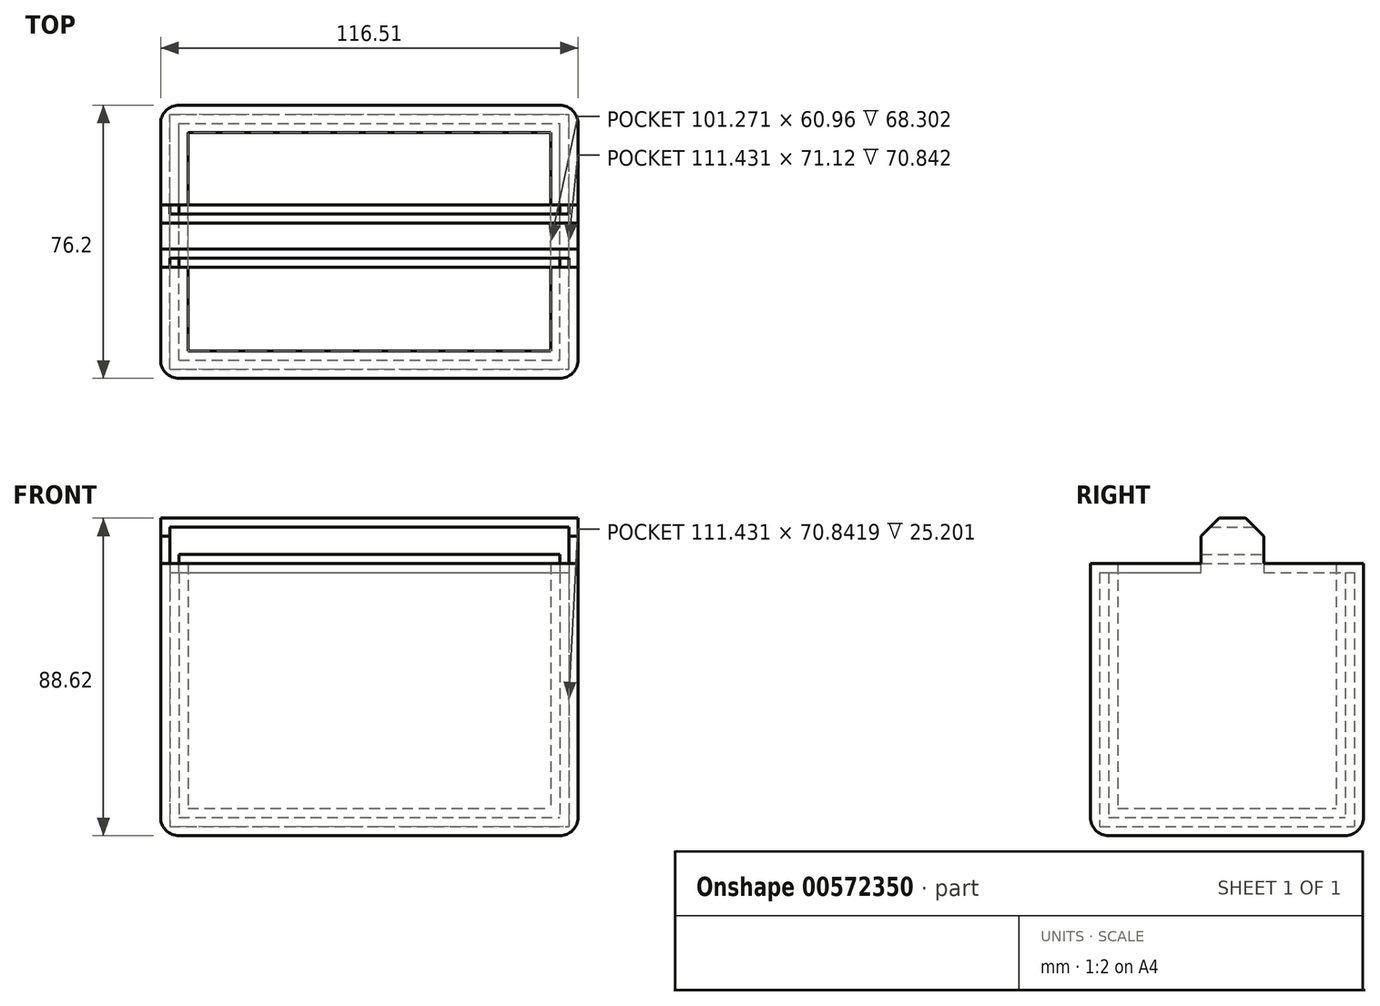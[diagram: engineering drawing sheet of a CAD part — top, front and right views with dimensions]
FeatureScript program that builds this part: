
annotation { "Feature Type Name" : "Feature", "Feature Type Description" : "" }
export const myFeature = defineFeature(function(context is Context, id is Id, definition is map)
    precondition{}
    {
        {
            var Q0;
            Q0=qCreatedBy(makeId("Front.planeOp"),FACE);
            var sketch = newSketch(context, id + "F0", { "sketchPlane" : qUnion([Q0])});
            skLineSegment(sketch, "E0.bottom", {"start": v(-51.4, 55.19) * mm, "end": v(65.12, 55.19) * mm});
            skLineSegment(sketch, "E0.top", {"start": v(-51.4, -20.73) * mm, "end": v(65.12, -20.73) * mm});
            skLineSegment(sketch, "E0.left", {"start": v(-51.4, 55.19) * mm, "end": v(-51.4, -20.73) * mm});
            skLineSegment(sketch, "E0.right", {"start": v(65.12, 55.19) * mm, "end": v(65.12, -20.73) * mm});
            skSolve(sketch);
        }
        {
            var Q0;
            Q0=makeQuery(id+"F0.imprint","IMPRINT",FACE,{"disambiguationData":[TD([[makeQuery(id+"F0.imprint","IMPRINT",EDGE,{"derivedFrom":sQuery(id+"F0.wireOp",EDGE,"E0.bottom")}),-1.0]])]});
            extrude(context, id + "F1", {"entities" : qUnion([Q0]), "depth" : 76.2 * mm, "offsetDistance" : 25.4 * mm});
        }
        {
            var Q0;
            Q0=makeQuery(id+"F1.opExtrude","SWEPT_FACE",FACE,{"disambiguationData":[OSD([sQuery(id+"F0.wireOp",EDGE,"E0.bottom")])]});
            shell(context, id + "F2", {"entities" : qUnion([Q0]), "thickness" : 7.62 * mm});
        }
        {
            var Q0;
            Q0=makeQuery(id+"F1.opExtrude","SWEPT_FACE",FACE,{"disambiguationData":[OSD([sQuery(id+"F0.wireOp",EDGE,"E0.bottom")])]});
            var sketch = newSketch(context, id + "F3", { "sketchPlane" : qUnion([Q0])});
            skLineSegment(sketch, "E1.bottom", {"start": v(-51.4, -27.74) * mm, "end": v(65.12, -27.74) * mm});
            skLineSegment(sketch, "E1.top", {"start": v(-51.4, -45.26) * mm, "end": v(65.12, -45.26) * mm});
            skLineSegment(sketch, "E1.left", {"start": v(-51.4, -27.74) * mm, "end": v(-51.4, -45.26) * mm});
            skLineSegment(sketch, "E1.right", {"start": v(65.12, -27.74) * mm, "end": v(65.12, -45.26) * mm});
            skSolve(sketch);
        }
        {
            var Q0;
            Q0 = qSketchRegion(id + "F3", true);
            extrude(context, id + "F4", {"entities" : qUnion([Q0]), "operationType" : NewBodyOperationType.ADD, "depth" : 12.7 * mm, "offsetDistance" : 25.4 * mm});
        }
        {
            var Q0;
            Q0=makeQuery(id+"F4.opExtrude","SWEPT_FACE",FACE,{"disambiguationData":[OSD([sQuery(id+"F3.wireOp",EDGE,"E1.top")])]});
            var Q1;
            Q1=makeQuery(id+"F4.opExtrude","SWEPT_FACE",FACE,{"disambiguationData":[OSD([sQuery(id+"F3.wireOp",EDGE,"E1.bottom")])]});
            shell(context, id + "F5", {"entities" : qUnion([Q0, Q1]), "thickness" : 2.54 * mm});
        }
        {
            var Q0;
            Q0=makeQuery(id+"F1.opExtrude","CAP_EDGE",EDGE,{"disambiguationData":[OSD([sQuery(id+"F0.wireOp",EDGE,"E0.right")])],"isStart":true});
            fillet(context, id + "F6", {"entities" : qUnion([Q0]), "radius" : 5.08 * mm, "tangentPropagation" : true, "allowEdgeOverflow" : false});
        }
        {
            var Q0;
            Q0=makeQuery(id+"F1.opExtrude","CAP_EDGE",EDGE,{"disambiguationData":[OSD([sQuery(id+"F0.wireOp",EDGE,"E0.top")])],"isStart":true});
            var Q1;
            Q1=makeQuery(id+"F1.opExtrude","CAP_EDGE",EDGE,{"disambiguationData":[OSD([sQuery(id+"F0.wireOp",EDGE,"E0.left")])],"isStart":true});
            fillet(context, id + "F7", {"entities" : qUnion([Q0, Q1]), "radius" : 5.08 * mm, "tangentPropagation" : true, "allowEdgeOverflow" : false});
        }
        {
            var Q0;
            Q0=makeQuery(id+"F1.opExtrude","CAP_EDGE",EDGE,{"disambiguationData":[OSD([sQuery(id+"F0.wireOp",EDGE,"E0.left")])],"isStart":false});
            fillet(context, id + "F8", {"entities" : qUnion([Q0]), "radius" : 5.08 * mm, "tangentPropagation" : true, "allowEdgeOverflow" : false});
        }
        {
            var Q0;
            Q0=makeQuery(id+"F1.opExtrude","SWEPT_EDGE",EDGE,{"disambiguationData":[OSD([sQuery(id+"F0.wireOp",EDGE,"E0.top"),sQuery(id+"F0.wireOp",EDGE,"E0.left")])]});
            fillet(context, id + "F9", {"entities" : qUnion([Q0]), "radius" : 5.08 * mm, "tangentPropagation" : true, "allowEdgeOverflow" : false});
        }
        {
            var Q0;
            Q0=makeQuery(id+"F4.opExtrude","CAP_EDGE",EDGE,{"disambiguationData":[OSD([sQuery(id+"F3.wireOp",EDGE,"E1.top")])],"isStart":false});
            chamfer(context, id + "F10", {"entities" : qUnion([Q0]), "width" : 5.08 * mm, "tangentPropagation" : true});
        }
        {
            var Q0;
            Q0=makeQuery(id+"F4.opExtrude","CAP_EDGE",EDGE,{"disambiguationData":[OSD([sQuery(id+"F3.wireOp",EDGE,"E1.bottom")])],"isStart":false});
            chamfer(context, id + "F11", {"entities" : qUnion([Q0]), "width" : 5.08 * mm, "tangentPropagation" : true});
        }
    });
